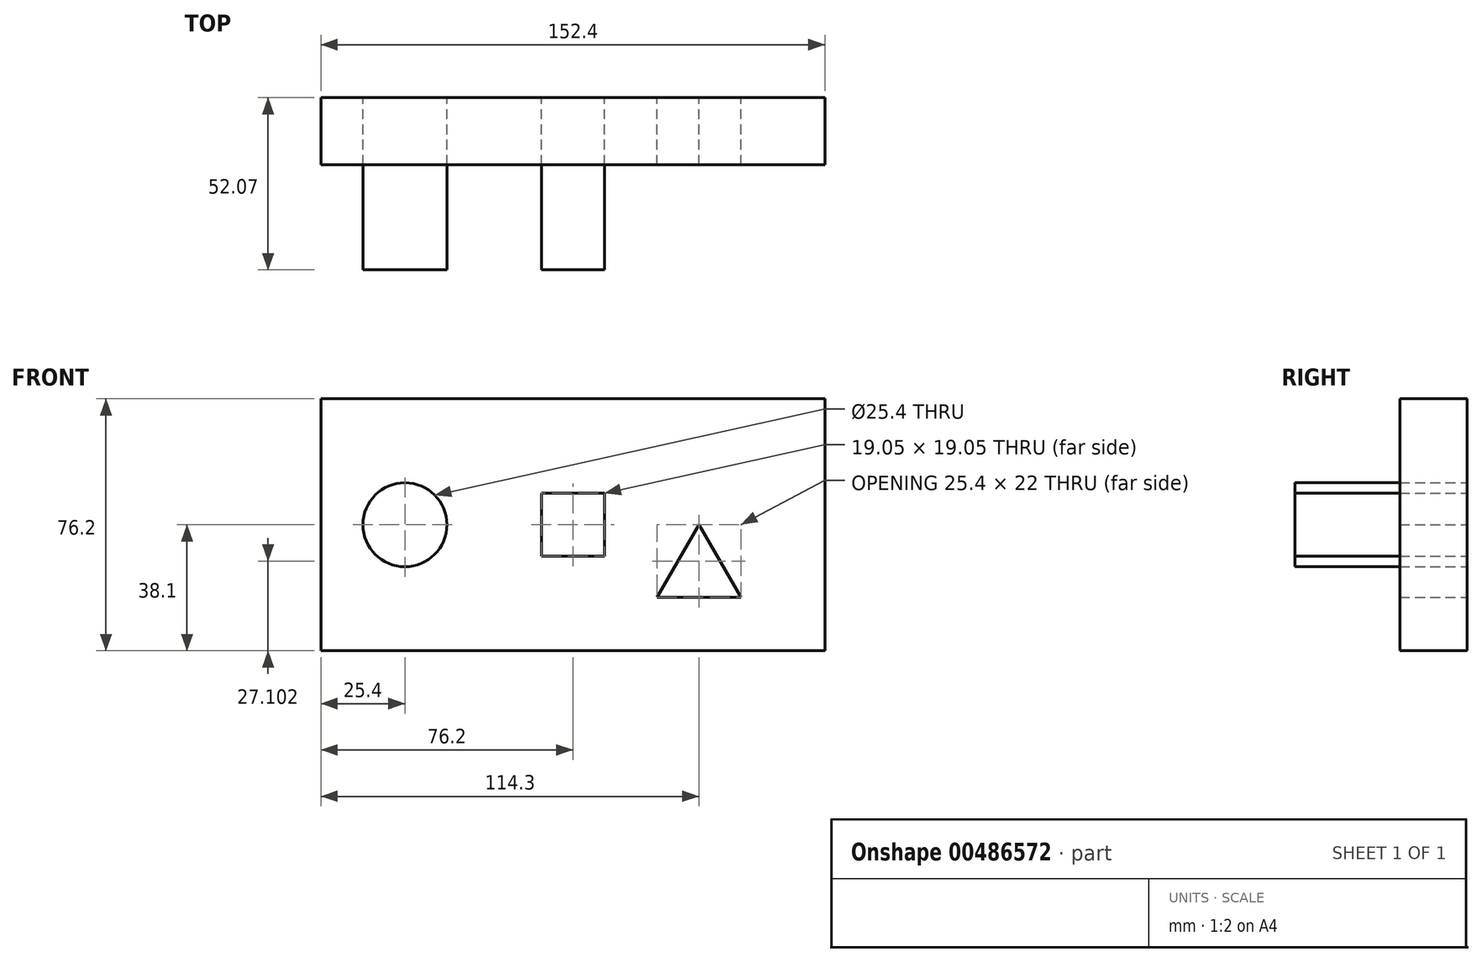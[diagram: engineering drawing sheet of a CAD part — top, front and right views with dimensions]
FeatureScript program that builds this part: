
annotation { "Feature Type Name" : "Feature", "Feature Type Description" : "" }
export const myFeature = defineFeature(function(context is Context, id is Id, definition is map)
    precondition{}
    {
        {
            var Q0;
            Q0=qCreatedBy(makeId("Front.planeOp"),FACE);
            var sketch = newSketch(context, id + "F0", { "sketchPlane" : qUnion([Q0])});
            skLineSegment(sketch, "E0", {"start": v(0, 0) * mm, "end": v(-31.75, 0) * mm});
            skLineSegment(sketch, "E1.bottom", {"start": v(44.45, 38.1) * mm, "end": v(-107.95, 38.1) * mm});
            skLineSegment(sketch, "E1.top", {"start": v(44.45, -38.1) * mm, "end": v(-107.95, -38.1) * mm});
            skLineSegment(sketch, "E1.left", {"start": v(44.45, 38.1) * mm, "end": v(44.45, -38.1) * mm});
            skLineSegment(sketch, "E1.right", {"start": v(-107.95, 38.1) * mm, "end": v(-107.95, -38.1) * mm});
            skPoint(sketch, "E1.middle", {"position": v(-31.75, 0) * mm});
            skLineSegment(sketch, "E2", {"start": v(0, 0) * mm, "end": v(6.35, 0) * mm});
            skLineSegment(sketch, "E3", {"start": v(6.35, 0) * mm, "end": v(19.05, -22) * mm});
            skLineSegment(sketch, "E4", {"start": v(19.05, -22) * mm, "end": v(-6.35, -22) * mm});
            skLineSegment(sketch, "E5", {"start": v(-6.35, -22) * mm, "end": v(6.35, 0) * mm});
            skLineSegment(sketch, "E6.bottom", {"start": v(-22.22, 9.53) * mm, "end": v(-41.27, 9.53) * mm});
            skLineSegment(sketch, "E6.top", {"start": v(-22.23, -9.52) * mm, "end": v(-41.27, -9.52) * mm});
            skLineSegment(sketch, "E6.left", {"start": v(-22.22, 9.53) * mm, "end": v(-22.22, -9.52) * mm});
            skLineSegment(sketch, "E6.right", {"start": v(-41.27, 9.53) * mm, "end": v(-41.27, -9.52) * mm});
            skLineSegment(sketch, "E7", {"start": v(-31.75, 0) * mm, "end": v(-82.55, 0) * mm});
            skCircle(sketch, "E8", {"center": v(-82.55, 0) * mm, "radius": 12.7 * mm});
            skSolve(sketch);
        }
        {
            var Q0;
            Q0=makeQuery(id+"F0.imprint","IMPRINT",FACE,{"disambiguationData":[TD([[makeQuery(id+"F0.imprint","IMPRINT",EDGE,{"derivedFrom":sQuery(id+"F0.wireOp",EDGE,"E1.bottom")}),1.0]])]});
            extrude(context, id + "F1", {"entities" : qUnion([Q0]), "depth" : 20.32 * mm});
        }
        {
            var Q0;
            Q0=makeQuery(id+"F0.imprint","IMPRINT",FACE,{"disambiguationData":[TD([[makeQuery(id+"F0.imprint","IMPRINT",EDGE,{"derivedFrom":sQuery(id+"F0.wireOp",EDGE,"E8")}),1.0]])]});
            var Q1;
            {var subQ1=sQuery(id+"F0.wireOp",EDGE,"E6.bottom");Q1=makeQuery(id+"F0.imprint","IMPRINT",FACE,{"disambiguationData":[TD([[makeQuery(id+"F0.imprint","IMPRINT",EDGE,{"derivedFrom":subQ1}),1.0]])]});}
            var Q2;
            {var subQ1=sQuery(id+"F0.wireOp",EDGE,"E6.top");Q2=makeQuery(id+"F0.imprint","IMPRINT",FACE,{"disambiguationData":[TD([[makeQuery(id+"F0.imprint","IMPRINT",EDGE,{"derivedFrom":subQ1}),-1.0]])]});}
            extrude(context, id + "F2", {"entities" : qUnion([Q0, Q1, Q2]), "depth" : 52.07 * mm});
        }
    });
